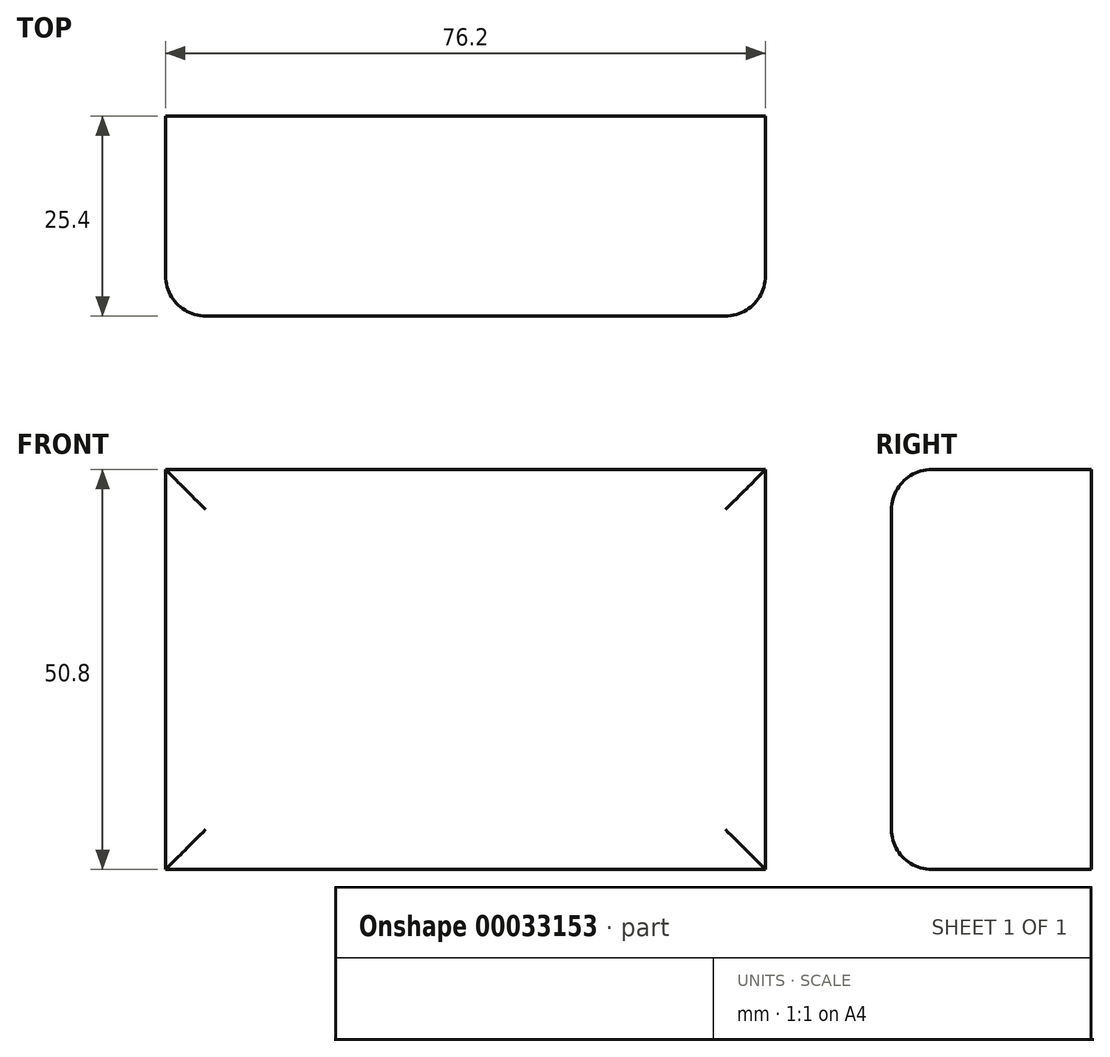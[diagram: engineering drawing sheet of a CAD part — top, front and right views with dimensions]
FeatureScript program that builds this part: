
annotation { "Feature Type Name" : "Feature", "Feature Type Description" : "" }
export const myFeature = defineFeature(function(context is Context, id is Id, definition is map)
    precondition{}
    {
        {
            var Q0;
            Q0=qCreatedBy(makeId("Front.planeOp"),FACE);
            var sketch = newSketch(context, id + "F0", { "sketchPlane" : qUnion([Q0])});
            skLineSegment(sketch, "E0.bottom", {"start": v(0, 0) * mm, "end": v(76.2, 0) * mm});
            skLineSegment(sketch, "E0.top", {"start": v(0, 50.8) * mm, "end": v(76.2, 50.8) * mm});
            skLineSegment(sketch, "E0.left", {"start": v(0, 0) * mm, "end": v(0, 50.8) * mm});
            skLineSegment(sketch, "E0.right", {"start": v(76.2, 0) * mm, "end": v(76.2, 50.8) * mm});
            skSolve(sketch);
        }
        {
            var Q0;
            Q0 = qSketchRegion(id + "F0", true);
            extrude(context, id + "F1", {"entities" : qUnion([Q0]), "oppositeDirection" : true, "depth" : 25.4 * mm});
        }
        {
            var Q0;
            Q0=makeQuery(id+"F1.opExtrude","CAP_FACE",FACE,{"disambiguationData":[OSD([sQuery(id+"F0.wireOp",EDGE,"E0.bottom"),sQuery(id+"F0.wireOp",EDGE,"E0.top"),sQuery(id+"F0.wireOp",EDGE,"E0.left"),sQuery(id+"F0.wireOp",EDGE,"E0.right")])],"isStart":true});
            fillet(context, id + "F2", {"entities" : qUnion([Q0]), "radius" : 5.08 * mm, "tangentPropagation" : true, "allowEdgeOverflow" : false});
        }
    });
